# Revit family: Grundplatten Typ I
name_source: partatom
category: HLS-Bauteile
revit_build: Autodesk Revit 2017 (Build: 20190507_1515(x64)
units: mm (PartAtom-declared; Revit-internal decimal feet)

## family parameters
Arbeitsebenenbasiert = Ja
Beim Laden mit Abzugskörper schneiden = Nein
Bemaßung runder Anschluss = Durchmesser verwenden
Gemeinsam genutzt = Ja
Immer vertikal = Nein
OmniClass-Nummer = 23.75.00.00
OmniClass-Titel = Climate Control (HVAC)
Raumberechnungspunkt = Nein
Teiletyp = Normal

## types (4) — shared parameters
Abstand zur Außenkante = 17 mm
Breite = 35 mm  [stored 0.114829 ft]
Firma = MEFA Befestigungs- und Montagesysteme GmbH
Höhe Gewindeanschluss HGW = 15 mm  [stored 0.0492126 ft]
Länge = 108 mm  [stored 0.354331 ft]
Stärke = 4 mm  [stored 0.0131234 ft]
zero-valued in all types: Sicherheitsfaktor, Vorgabe-Ansicht

## per-type parameters (varying)
| type | Abmessung | Anschluss | Anschlüsse | Anzahl Befestigungsloch | Artikelnummer | EAN | Fabrikat | Gewicht | Gewicht pro Bauteil | Kurztext1 | Kurztext2 | Langloch | Lochabstand längs | Material | Materialname | Mengeneinheit | Oberflaeche | max. zul. Last hängend | vpe |
| Grundplatte Typ I 108x35x4,0 M 8/M10 |  |  | 6kt-Mutter parametrik : Stufenmutter M8/M10 (0009820) |  | 0590044301 |  |  | 0.00 kg | 0.00 kg |  |  |  | 0 mm  [stored 0 ft] |  |  |  |  | 0.00 kN |  |
| Grundplatte Typ I 108x35x4,0 M12 |  |  | 6kt-Mutter parametrik : Hutmutter gedreht M12 (4130012) |  | 059006101 |  |  | 0.00 kg | 0.00 kg |  |  |  | 0 mm  [stored 0 ft] |  |  |  |  | 0.00 kN |  |
| Grundplatte Typ I 108x35x4,0 M16 |  |  | 6kt-Mutter parametrik : Hutmutter M16 (4130016) |  | 059008801 |  |  | 0.00 kg | 0.00 kg |  |  |  | 0 mm  [stored 0 ft] |  |  |  |  | 0.00 kN |  |
| Grundplatte Typ I 108x35x4,0 1/2" | 108 x 35 x 4 mm | 1/2'' | Runde Gewindeanschlusse parametrik : Muffe 1/2´´ (0009865) | 2 | 059004502 | 4250928449702 | MEFA | 0.14 kg | 0.14 kg | Grundplatte Typ I | Anschluss 1/2'' Platte 108x35x4 mm | 13x20 mm | 74 mm | Stahl | S235 | St | galvanisch verzinkt | 1.50 kN | 50 St |

note: [stored X ft] marks values corroborated as IEEE doubles in the binary element streams (Revit-internal decimal feet)

## geometry (parser evidence)
native form markers: Sweep x1
no freeform markers — native parametric forms only
